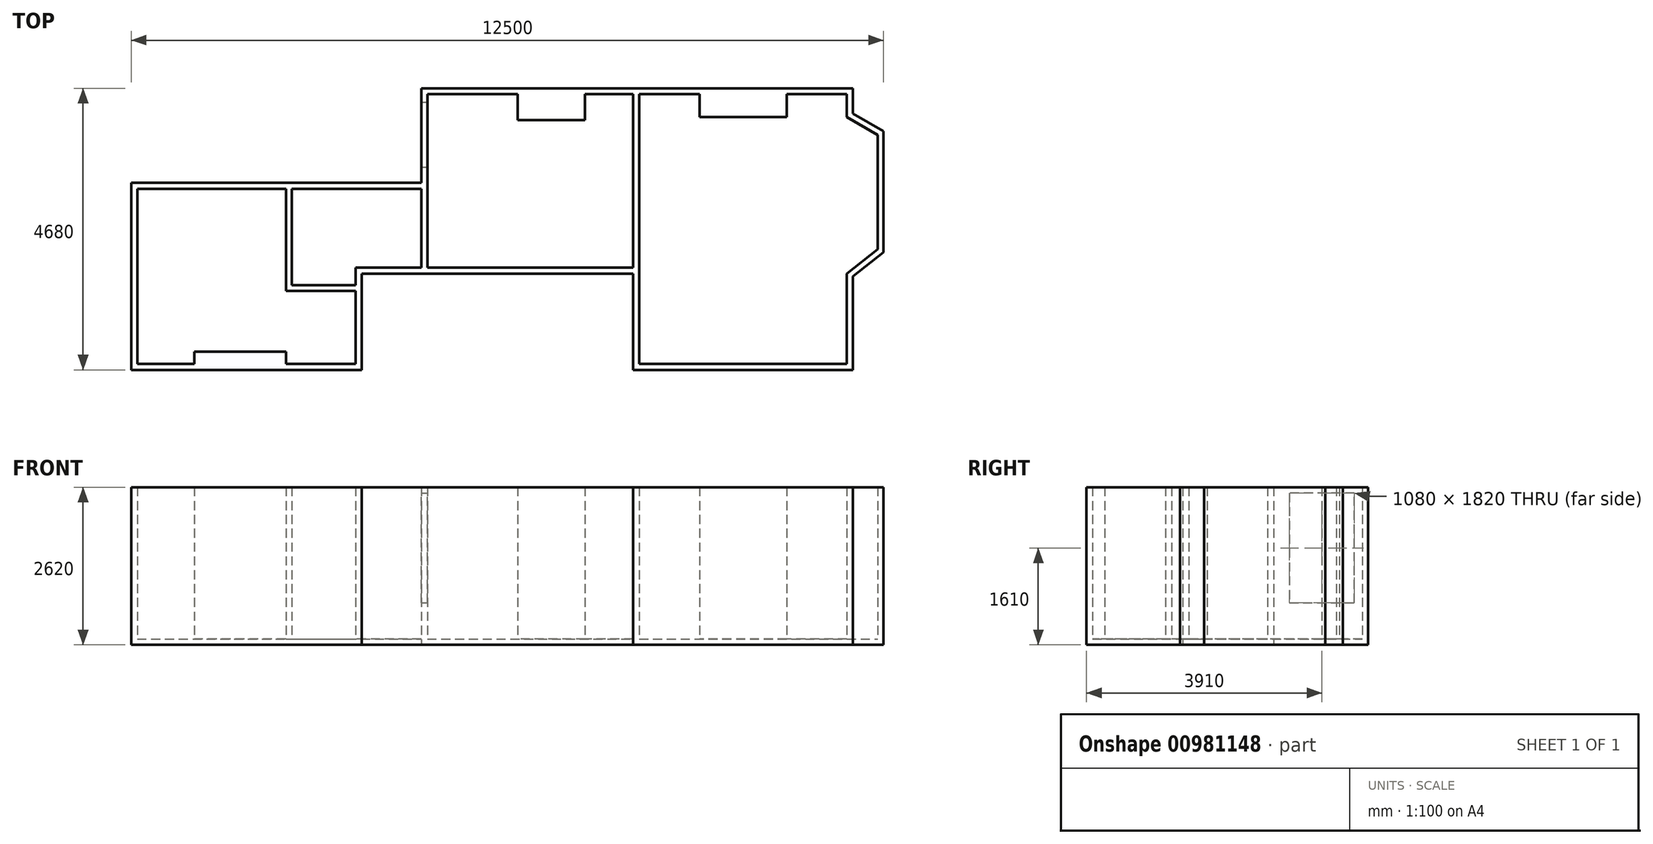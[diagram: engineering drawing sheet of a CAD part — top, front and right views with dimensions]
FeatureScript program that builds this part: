
annotation { "Feature Type Name" : "Feature", "Feature Type Description" : "" }
export const myFeature = defineFeature(function(context is Context, id is Id, definition is map)
    precondition{}
    {
        {
            var Q0;
            Q0=qCreatedBy(makeId("Top.planeOp"),FACE);
            var sketch = newSketch(context, id + "F0", { "sketchPlane" : qUnion([Q0])});
            skLineSegment(sketch, "E0", {"start": v(0, 500) * mm, "end": v(950, 500) * mm});
            skLineSegment(sketch, "E1", {"start": v(950, 500) * mm, "end": v(950, 700) * mm});
            skLineSegment(sketch, "E2", {"start": v(0, 500) * mm, "end": v(0, 3410) * mm});
            skLineSegment(sketch, "E3", {"start": v(0, 3410) * mm, "end": v(2470, 3410) * mm});
            skLineSegment(sketch, "E4", {"start": v(2470, 3410) * mm, "end": v(2470, 1910) * mm});
            skLineSegment(sketch, "E5", {"start": v(3630, 500) * mm, "end": v(2470, 500) * mm});
            skLineSegment(sketch, "E6", {"start": v(2470, 500) * mm, "end": v(2470, 700) * mm});
            skLineSegment(sketch, "E7", {"start": v(2470, 700) * mm, "end": v(950, 700) * mm});
            skLineSegment(sketch, "E8.0", {"start": v(-100, 400) * mm, "end": v(-100, 3510) * mm});
            skLineSegment(sketch, "E8.1", {"start": v(-100, 400) * mm, "end": v(3250, 400) * mm});
            skLineSegment(sketch, "E8.5", {"start": v(-100, 3510) * mm, "end": v(2570, 3510) * mm});
            skLineSegment(sketch, "E8.6", {"start": v(3730, 400) * mm, "end": v(3250, 400) * mm});
            skLineSegment(sketch, "E9", {"start": v(4720, 1994.9) * mm, "end": v(4720, 2000) * mm});
            skLineSegment(sketch, "E10", {"start": v(4820, 2100) * mm, "end": v(4820, 4980) * mm});
            skLineSegment(sketch, "E11", {"start": v(4820, 4980) * mm, "end": v(6320, 4980) * mm});
            skLineSegment(sketch, "E12", {"start": v(6320, 4980) * mm, "end": v(6320, 4550) * mm});
            skLineSegment(sketch, "E13", {"start": v(4820, 2100) * mm, "end": v(8240, 2100) * mm});
            skLineSegment(sketch, "E14", {"start": v(8240, 2100) * mm, "end": v(8240, 4980) * mm});
            skLineSegment(sketch, "E15", {"start": v(8240, 4980) * mm, "end": v(7440, 4980) * mm});
            skLineSegment(sketch, "E16", {"start": v(7440, 4980) * mm, "end": v(7440, 4550) * mm});
            skLineSegment(sketch, "E17", {"start": v(7440, 4550) * mm, "end": v(6320, 4550) * mm});
            skLineSegment(sketch, "E18", {"start": v(8340, 4980) * mm, "end": v(9340, 4980) * mm});
            skLineSegment(sketch, "E19", {"start": v(9340, 4980) * mm, "end": v(9340, 4600) * mm});
            skLineSegment(sketch, "E20", {"start": v(8340, 4980) * mm, "end": v(8340, 500) * mm});
            skLineSegment(sketch, "E21", {"start": v(8340, 500) * mm, "end": v(11790, 500) * mm});
            skLineSegment(sketch, "E22", {"start": v(11790, 500) * mm, "end": v(11790, 2000) * mm});
            skLineSegment(sketch, "E23", {"start": v(11790, 2000) * mm, "end": v(12300, 2401.54) * mm});
            skLineSegment(sketch, "E24", {"start": v(11790, 4980) * mm, "end": v(10790, 4980) * mm});
            skLineSegment(sketch, "E25", {"start": v(10790, 4980) * mm, "end": v(10790, 4600) * mm});
            skLineSegment(sketch, "E26", {"start": v(10790, 4600) * mm, "end": v(9340, 4600) * mm});
            skLineSegment(sketch, "E27", {"start": v(9340, 4600) * mm, "end": v(10790, 4600) * mm});
            skLineSegment(sketch, "E28", {"start": v(12300, 4305.55) * mm, "end": v(12300, 2401.54) * mm});
            skLineSegment(sketch, "E29", {"start": v(11790, 4980) * mm, "end": v(11790, 4600) * mm});
            skLineSegment(sketch, "E30", {"start": v(11790, 4600) * mm, "end": v(12300, 4305.55) * mm});
            skPoint(sketch, "E31.orphan", {"position": v(12300, 4600) * mm});
            skPoint(sketch, "E32.orphan", {"position": v(8340, 4600) * mm});
            skLineSegment(sketch, "E33", {"start": v(4720, 3010) * mm, "end": v(4720, 4980) * mm});
            skLineSegment(sketch, "E34", {"start": v(4720, 4980) * mm, "end": v(4720, 5080) * mm});
            skLineSegment(sketch, "E35", {"start": v(4720, 5080) * mm, "end": v(11790, 5080) * mm});
            skLineSegment(sketch, "E36", {"start": v(11790, 5080) * mm, "end": v(11890, 5080) * mm});
            skLineSegment(sketch, "E37.0", {"start": v(11890, 1951.46) * mm, "end": v(12400, 2353) * mm});
            skLineSegment(sketch, "E37.1", {"start": v(12400, 4363.29) * mm, "end": v(12400, 2353) * mm});
            skLineSegment(sketch, "E37.2", {"start": v(11890, 4657.74) * mm, "end": v(12400, 4363.29) * mm});
            skLineSegment(sketch, "E38", {"start": v(11890, 5080) * mm, "end": v(11890, 4657.74) * mm});
            skLineSegment(sketch, "E39.0", {"start": v(11890, 400) * mm, "end": v(11890, 1951.46) * mm});
            skLineSegment(sketch, "E39.1", {"start": v(8316.84, 400) * mm, "end": v(11890, 400) * mm});
            skLineSegment(sketch, "E40", {"start": v(8240, 2000) * mm, "end": v(8240, 400) * mm});
            skLineSegment(sketch, "E41", {"start": v(11890, 400) * mm, "end": v(8240, 400) * mm});
            skLineSegment(sketch, "E42", {"start": v(2570, 3510) * mm, "end": v(4720, 3510) * mm});
            skLineSegment(sketch, "E43", {"start": v(2570, 3410) * mm, "end": v(4720, 3410) * mm});
            skLineSegment(sketch, "E44", {"start": v(2570, 3410) * mm, "end": v(2570, 1810) * mm});
            skLineSegment(sketch, "E45", {"start": v(2570, 1710) * mm, "end": v(3630, 1710) * mm});
            skLineSegment(sketch, "E46", {"start": v(3730, 400) * mm, "end": v(3730, 2000) * mm});
            skLineSegment(sketch, "E47", {"start": v(3730, 2000) * mm, "end": v(8240, 2000) * mm});
            skLineSegment(sketch, "E48", {"start": v(3630, 1710) * mm, "end": v(3630, 500) * mm});
            skLineSegment(sketch, "E49", {"start": v(4720, 3010) * mm, "end": v(4720, 2100) * mm});
            skLineSegment(sketch, "E50", {"start": v(4720, 2100) * mm, "end": v(3630, 2100) * mm});
            skLineSegment(sketch, "E51", {"start": v(3630, 2100) * mm, "end": v(3630, 1810) * mm});
            skLineSegment(sketch, "E52", {"start": v(2470, 1910) * mm, "end": v(2470, 1710) * mm});
            skLineSegment(sketch, "E53", {"start": v(2470, 1710) * mm, "end": v(3630, 1710) * mm});
            skLineSegment(sketch, "E54", {"start": v(2470, 1710) * mm, "end": v(2470, 1810) * mm});
            skLineSegment(sketch, "E55", {"start": v(2570, 1810) * mm, "end": v(3630, 1810) * mm});
            skSolve(sketch);
        }
        {
            var Q0;
            Q0=makeQuery(id+"F0.imprint","IMPRINT",FACE,{"disambiguationData":[TD([[makeQuery(id+"F0.imprint","IMPRINT",EDGE,{"derivedFrom":sQuery(id+"F0.wireOp",EDGE,"E0")}),-1.0]])]});
            extrude(context, id + "F1", {"entities" : qUnion([Q0]), "depth" : 2520 * mm, "offsetDistance" : 25 * mm});
        }
        {
            var Q0;
            Q0=makeQuery(id+"F1.opExtrude","CAP_FACE",FACE,{"disambiguationData":[OSD([sQuery(id+"F0.wireOp",EDGE,"E0"),sQuery(id+"F0.wireOp",EDGE,"E1"),sQuery(id+"F0.wireOp",EDGE,"E2"),sQuery(id+"F0.wireOp",EDGE,"E3"),sQuery(id+"F0.wireOp",EDGE,"E4"),sQuery(id+"F0.wireOp",EDGE,"E5"),sQuery(id+"F0.wireOp",EDGE,"E6"),sQuery(id+"F0.wireOp",EDGE,"E7"),sQuery(id+"F0.wireOp",EDGE,"E8.0"),sQuery(id+"F0.wireOp",EDGE,"E8.1"),sQuery(id+"F0.wireOp",EDGE,"E8.5"),sQuery(id+"F0.wireOp",EDGE,"E8.6"),sQuery(id+"F0.wireOp",EDGE,"E10"),sQuery(id+"F0.wireOp",EDGE,"E11"),sQuery(id+"F0.wireOp",EDGE,"E12"),sQuery(id+"F0.wireOp",EDGE,"E13"),sQuery(id+"F0.wireOp",EDGE,"E14"),sQuery(id+"F0.wireOp",EDGE,"E15"),sQuery(id+"F0.wireOp",EDGE,"E16"),sQuery(id+"F0.wireOp",EDGE,"E17"),sQuery(id+"F0.wireOp",EDGE,"E18"),sQuery(id+"F0.wireOp",EDGE,"E19"),sQuery(id+"F0.wireOp",EDGE,"E20"),sQuery(id+"F0.wireOp",EDGE,"E21"),sQuery(id+"F0.wireOp",EDGE,"E22"),sQuery(id+"F0.wireOp",EDGE,"E23"),sQuery(id+"F0.wireOp",EDGE,"E24"),sQuery(id+"F0.wireOp",EDGE,"E25"),sQuery(id+"F0.wireOp",EDGE,"E27"),sQuery(id+"F0.wireOp",EDGE,"E28"),sQuery(id+"F0.wireOp",EDGE,"E29"),sQuery(id+"F0.wireOp",EDGE,"E30"),sQuery(id+"F0.wireOp",EDGE,"E33"),sQuery(id+"F0.wireOp",EDGE,"E34"),sQuery(id+"F0.wireOp",EDGE,"E35"),sQuery(id+"F0.wireOp",EDGE,"E36"),sQuery(id+"F0.wireOp",EDGE,"E37.0"),sQuery(id+"F0.wireOp",EDGE,"E37.1"),sQuery(id+"F0.wireOp",EDGE,"E37.2"),sQuery(id+"F0.wireOp",EDGE,"E38"),sQuery(id+"F0.wireOp",EDGE,"E39.0"),sQuery(id+"F0.wireOp",EDGE,"E40"),sQuery(id+"F0.wireOp",EDGE,"E41"),sQuery(id+"F0.wireOp",EDGE,"E42"),sQuery(id+"F0.wireOp",EDGE,"E43"),sQuery(id+"F0.wireOp",EDGE,"E44"),sQuery(id+"F0.wireOp",EDGE,"E46"),sQuery(id+"F0.wireOp",EDGE,"E47"),sQuery(id+"F0.wireOp",EDGE,"E48"),sQuery(id+"F0.wireOp",EDGE,"E49"),sQuery(id+"F0.wireOp",EDGE,"E50"),sQuery(id+"F0.wireOp",EDGE,"E51"),sQuery(id+"F0.wireOp",EDGE,"E52"),sQuery(id+"F0.wireOp",EDGE,"E53"),sQuery(id+"F0.wireOp",EDGE,"E54"),sQuery(id+"F0.wireOp",EDGE,"E55")])],"isStart":true});
            var sketch = newSketch(context, id + "F2", { "sketchPlane" : qUnion([Q0])});
            skLineSegment(sketch, "E56.0", {"start": v(4720, -5080) * mm, "end": v(11890, -5080) * mm});
            skLineSegment(sketch, "E57", {"start": v(4720, -5080) * mm, "end": v(4720, -3510) * mm});
            skLineSegment(sketch, "E58", {"start": v(4720, -3510) * mm, "end": v(-100, -3510) * mm});
            skLineSegment(sketch, "E59", {"start": v(-100, -3510) * mm, "end": v(-100, -400) * mm});
            skLineSegment(sketch, "E60", {"start": v(-100, -400) * mm, "end": v(3730, -400) * mm});
            skLineSegment(sketch, "E61", {"start": v(3730, -400) * mm, "end": v(3730, -2000) * mm});
            skLineSegment(sketch, "E62", {"start": v(3730, -2000) * mm, "end": v(8240, -2000) * mm});
            skLineSegment(sketch, "E63", {"start": v(8240, -2000) * mm, "end": v(8240, -400) * mm});
            skLineSegment(sketch, "E64", {"start": v(8240, -400) * mm, "end": v(11890, -400) * mm});
            skLineSegment(sketch, "E65", {"start": v(11890, -400) * mm, "end": v(11890, -1951.46) * mm});
            skLineSegment(sketch, "E66", {"start": v(11890, -1951.46) * mm, "end": v(12400, -2353) * mm});
            skLineSegment(sketch, "E67", {"start": v(12400, -2353) * mm, "end": v(12400, -4363.29) * mm});
            skLineSegment(sketch, "E68", {"start": v(12400, -4363.29) * mm, "end": v(11890, -4657.74) * mm});
            skLineSegment(sketch, "E69", {"start": v(11890, -4657.74) * mm, "end": v(11890, -5080) * mm});
            skSolve(sketch);
        }
        {
            var Q0;
            Q0 = qSketchRegion(id + "F2", true);
            extrude(context, id + "F3", {"entities" : qUnion([Q0]), "operationType" : NewBodyOperationType.ADD, "depth" : 100 * mm, "offsetDistance" : 25 * mm});
        }
        {
            var Q0;
            Q0=makeQuery(id+"F1.opExtrude","SWEPT_FACE",FACE,{"disambiguationData":[OSD([sQuery(id+"F0.wireOp",EDGE,"E10")])]});
            var sketch = newSketch(context, id + "F4", { "sketchPlane" : qUnion([Q0])});
            skLineSegment(sketch, "E70", {"start": v(2100, 0) * mm, "end": v(3770, 0) * mm, "construction": true});
            skLineSegment(sketch, "E71", {"start": v(3770, 0) * mm, "end": v(3770, 600) * mm, "construction": true});
            skLineSegment(sketch, "E72", {"start": v(3770, 600) * mm, "end": v(4850, 600) * mm});
            skLineSegment(sketch, "E73", {"start": v(4850, 600) * mm, "end": v(4850, 2420) * mm});
            skLineSegment(sketch, "E74", {"start": v(4850, 2420) * mm, "end": v(3770, 2420) * mm});
            skLineSegment(sketch, "E75", {"start": v(3770, 2420) * mm, "end": v(3770, 600) * mm});
            skSolve(sketch);
        }
        {
            var Q0;
            Q0 = qSketchRegion(id + "F4", true);
            extrude(context, id + "F5", {"entities" : qUnion([Q0]), "operationType" : NewBodyOperationType.REMOVE, "endBound" : BoundingType.UP_TO_NEXT, "oppositeDirection" : true, "depth" : 25 * mm, "offsetDistance" : 25 * mm});
        }
    });
